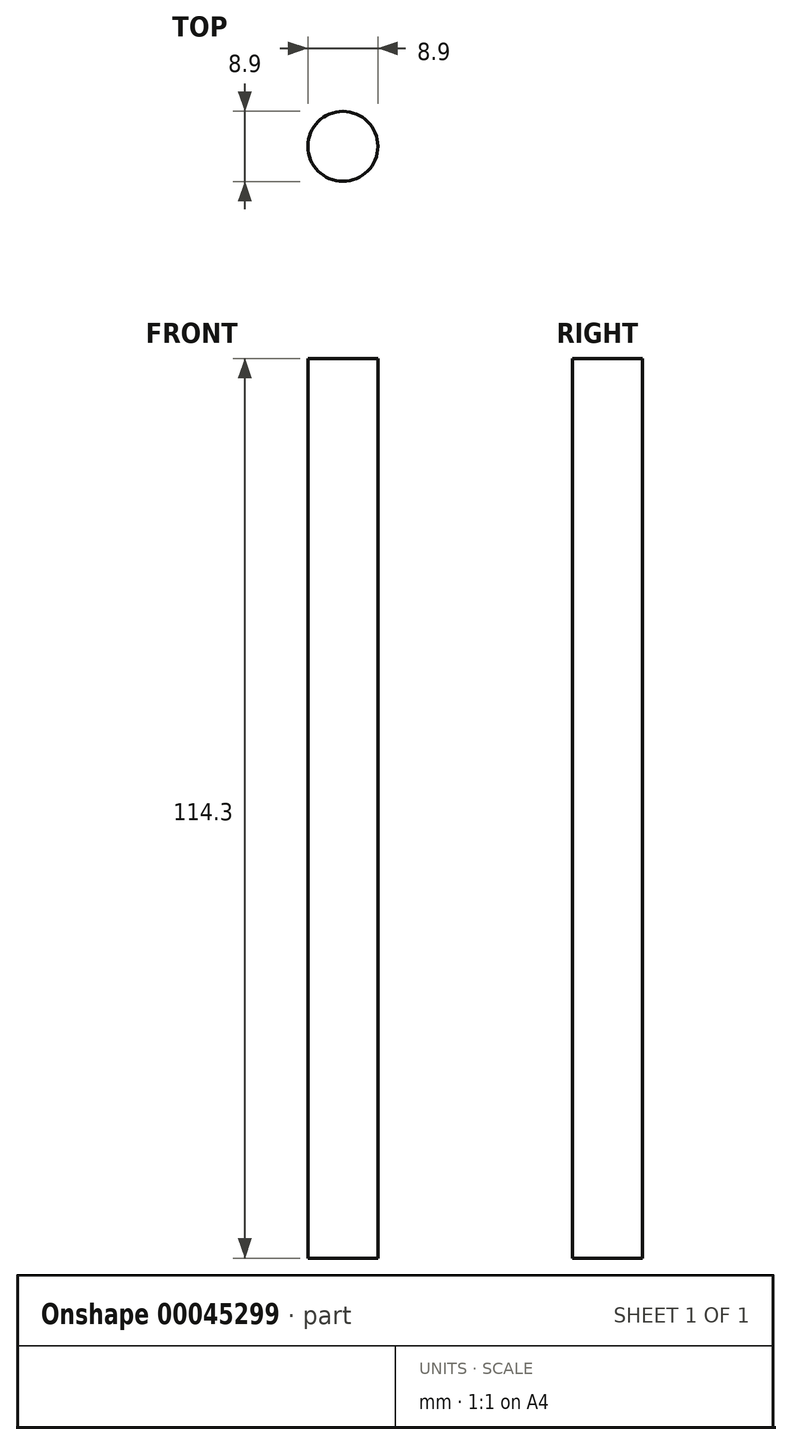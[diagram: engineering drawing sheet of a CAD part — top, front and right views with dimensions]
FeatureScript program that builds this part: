
annotation { "Feature Type Name" : "Feature", "Feature Type Description" : "" }
export const myFeature = defineFeature(function(context is Context, id is Id, definition is map)
    precondition{}
    {
        {
            var Q0;
            Q0=qCreatedBy(makeId("Top.planeOp"),FACE);
            var sketch = newSketch(context, id + "F0", { "sketchPlane" : qUnion([Q0])});
            skCircle(sketch, "E0", {"center": v(0, 0) * mm, "radius": 4.45 * mm});
            skSolve(sketch);
        }
        {
            var Q0;
            Q0=makeQuery(id+"F0.imprint","IMPRINT",FACE,{"disambiguationData":[TD([[makeQuery(id+"F0.imprint","IMPRINT",EDGE,{"derivedFrom":sQuery(id+"F0.wireOp",EDGE,"E0")}),1.0]])]});
            extrude(context, id + "F1", {"entities" : qUnion([Q0]), "depth" : 114.3 * mm});
        }
    });
